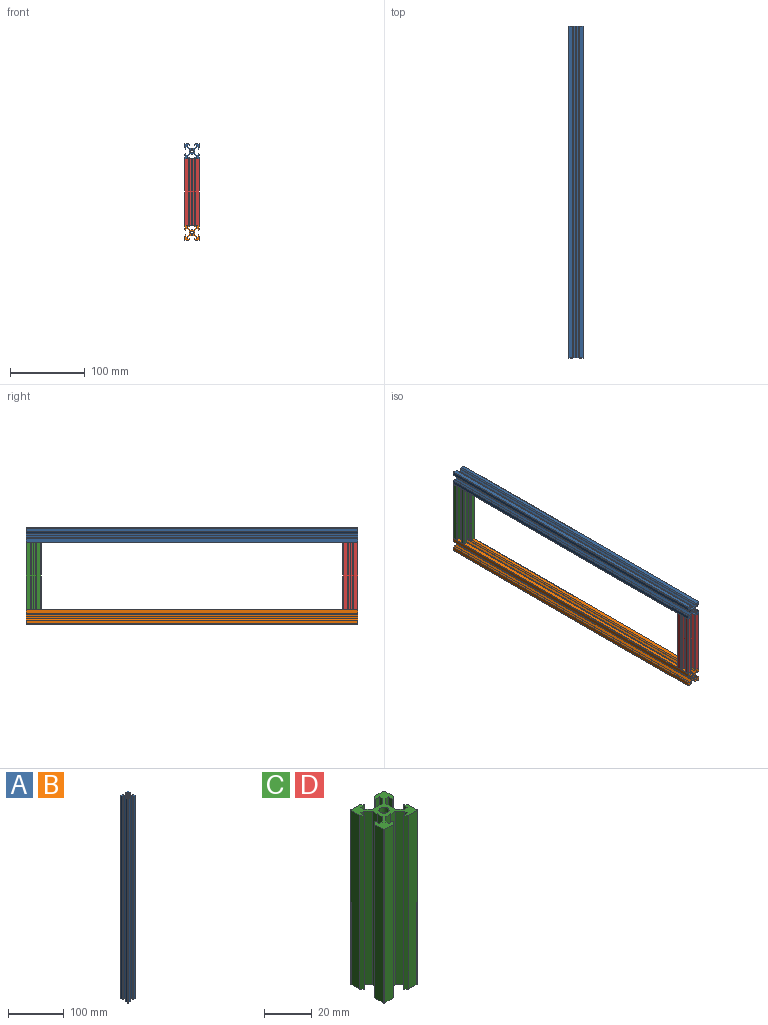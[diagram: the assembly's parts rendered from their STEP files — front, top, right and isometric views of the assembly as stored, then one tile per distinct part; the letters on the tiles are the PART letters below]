
ASSEMBLY  parts=4 mates=11
PART A: 71 faces, bbox 20x20x444.5 mm
  f0: cylinder r=2.1mm len=444.5mm, axis (0,0,-1), area 5865mm2, adj f69,f70
  f1: plane 444.5x0.21mm, normal (0.71,0.71,0), area 132mm2, adj f2,f68,f69,f70
  f2: plane 444.5x0.21mm, normal (0.71,-0.71,0), area 132mm2, adj f1,f3,f69,f70
  f3: plane 444.5x2.63mm, normal (1,0,0), area 1168.7mm2, adj f2,f4,f69,f70
  f4: plane 444.5x2.66mm, normal (0.71,-0.71,0), area 1672.5mm2, adj f3,f5,f69,f70
  f5: plane 444.5x1.64mm, normal (0,-1,0), area 728.7mm2, adj f4,f6,f69,f70
  f6: plane 444.5x2.38mm, normal (-1,0,0), area 1055.7mm2, adj f5,f7,f69,f70
  f7: plane 444.5x0.35mm, normal (0,-1,0), area 153.4mm2, adj f6,f8,f69,f70
  f8: plane 444.5x1.46mm, normal (0.71,-0.71,0), area 914.6mm2, adj f7,f9,f69,f70
  f9: plane 444.5x4.92mm, normal (1,0,0), area 2186.9mm2, adj f8,f10,f69,f70
  f10: cylinder r=0.5mm len=444.5mm, axis (0,0,-1), area 349.1mm2, adj f9,f11,f69,f70
  f11: plane 444.5x4.92mm, normal (0,1,0), area 2186.9mm2, adj f10,f12,f69,f70
  f12: plane 444.5x1.46mm, normal (-0.71,0.71,0), area 914.6mm2, adj f11,f13,f69,f70
  f13: plane 444.5x0.35mm, normal (-1,0,0), area 153.4mm2, adj f12,f14,f69,f70
  f14: plane 444.5x2.38mm, normal (0,-1,0), area 1055.7mm2, adj f13,f15,f69,f70
  f15: plane 444.5x1.64mm, normal (-1,0,0), area 728.7mm2, adj f14,f16,f69,f70
  f16: plane 444.5x2.66mm, normal (-0.71,0.71,0), area 1672.5mm2, adj f15,f17,f69,f70
  f17: plane 444.5x2.63mm, normal (0,1,0), area 1168.7mm2, adj f16,f18,f69,f70
  f18: plane 444.5x0.21mm, normal (-0.71,0.71,0), area 132mm2, adj f17,f19,f69,f70
  f19: plane 444.5x0.21mm, normal (0.71,0.71,0), area 132mm2, adj f18,f20,f69,f70
  f20: plane 444.5x2.63mm, normal (0,1,0), area 1168.7mm2, adj f19,f21,f69,f70
  f21: plane 444.5x2.66mm, normal (0.71,0.71,0), area 1672.5mm2, adj f20,f22,f69,f70
  f22: plane 444.5x1.64mm, normal (1,0,0), area 728.7mm2, adj f21,f23,f69,f70
  f23: plane 444.5x2.38mm, normal (0,-1,0), area 1055.7mm2, adj f22,f24,f69,f70
  f24: plane 444.5x0.35mm, normal (1,0,0), area 153.4mm2, adj f23,f25,f69,f70
  f25: plane 444.5x1.46mm, normal (0.71,0.71,0), area 914.6mm2, adj f24,f26,f69,f70
  f26: plane 444.5x4.92mm, normal (0,1,0), area 2186.9mm2, adj f25,f27,f69,f70
  f27: cylinder r=0.5mm len=444.5mm, axis (0,0,-1), area 349.1mm2, adj f26,f28,f69,f70
  f28: plane 444.5x4.92mm, normal (-1,0,0), area 2186.9mm2, adj f27,f29,f69,f70
  f29: plane 444.5x1.46mm, normal (-0.71,-0.71,0), area 914.6mm2, adj f28,f30,f69,f70
  f30: plane 444.5x0.35mm, normal (0,-1,0), area 153.4mm2, adj f29,f31,f69,f70
  f31: plane 444.5x2.38mm, normal (1,0,0), area 1055.7mm2, adj f30,f32,f69,f70
  f32: plane 444.5x1.64mm, normal (0,-1,0), area 728.7mm2, adj f31,f33,f69,f70
  f33: plane 444.5x2.66mm, normal (-0.71,-0.71,0), area 1672.5mm2, adj f32,f34,f69,f70
  f34: plane 444.5x2.63mm, normal (-1,0,0), area 1168.7mm2, adj f33,f35,f69,f70
  f35: plane 444.5x0.21mm, normal (-0.71,-0.71,0), area 132mm2, adj f34,f36,f69,f70
  f36: plane 444.5x0.21mm, normal (-0.71,0.71,0), area 132mm2, adj f35,f37,f69,f70
  f37: plane 444.5x2.63mm, normal (-1,0,0), area 1168.7mm2, adj f36,f38,f69,f70
  f38: plane 444.5x2.66mm, normal (-0.71,0.71,0), area 1672.5mm2, adj f37,f39,f69,f70
  f39: plane 444.5x1.64mm, normal (0,1,0), area 728.7mm2, adj f38,f40,f69,f70
  f40: plane 444.5x2.38mm, normal (1,0,0), area 1055.7mm2, adj f39,f41,f69,f70
  f41: plane 444.5x0.35mm, normal (0,1,0), area 153.4mm2, adj f40,f42,f69,f70
  f42: plane 444.5x1.46mm, normal (-0.71,0.71,0), area 914.6mm2, adj f41,f43,f69,f70
  f43: plane 444.5x4.92mm, normal (-1,0,0), area 2186.9mm2, adj f42,f44,f69,f70
  f44: cylinder r=0.5mm len=444.5mm, axis (0,0,-1), area 349.1mm2, adj f43,f45,f69,f70
  f45: plane 444.5x4.92mm, normal (0,-1,0), area 2186.9mm2, adj f44,f46,f69,f70
  f46: plane 444.5x1.46mm, normal (0.71,-0.71,0), area 914.6mm2, adj f45,f47,f69,f70
  f47: plane 444.5x0.35mm, normal (1,0,0), area 153.4mm2, adj f46,f48,f69,f70
  f48: plane 444.5x2.38mm, normal (0,1,0), area 1055.7mm2, adj f47,f49,f69,f70
  f49: plane 444.5x1.64mm, normal (1,0,0), area 728.7mm2, adj f48,f50,f69,f70
  f50: plane 444.5x2.66mm, normal (0.71,-0.71,0), area 1672.5mm2, adj f49,f51,f69,f70
  f51: plane 444.5x2.63mm, normal (0,-1,0), area 1168.7mm2, adj f50,f52,f69,f70
  f52: plane 444.5x0.21mm, normal (0.71,-0.71,0), area 132mm2, adj f51,f53,f69,f70
  f53: plane 444.5x0.21mm, normal (-0.71,-0.71,0), area 132mm2, adj f52,f54,f69,f70
  f54: plane 444.5x2.63mm, normal (0,-1,0), area 1168.7mm2, adj f53,f55,f69,f70
  f55: plane 444.5x2.66mm, normal (-0.71,-0.71,0), area 1672.5mm2, adj f54,f56,f69,f70
  f56: plane 444.5x1.64mm, normal (-1,0,0), area 728.7mm2, adj f55,f57,f69,f70
  f57: plane 444.5x2.38mm, normal (0,1,0), area 1055.7mm2, adj f56,f58,f69,f70
  f58: plane 444.5x0.35mm, normal (-1,0,0), area 153.4mm2, adj f57,f59,f69,f70
  f59: plane 444.5x1.46mm, normal (-0.71,-0.71,0), area 914.6mm2, adj f58,f60,f69,f70
  f60: plane 444.5x4.92mm, normal (0,-1,0), area 2186.9mm2, adj f59,f61,f69,f70
  f61: cylinder r=0.5mm len=444.5mm, axis (0,0,-1), area 349.1mm2, adj f60,f62,f69,f70
  f62: plane 444.5x4.92mm, normal (1,0,0), area 2186.9mm2, adj f61,f63,f69,f70
  f63: plane 444.5x1.46mm, normal (0.71,0.71,0), area 914.6mm2, adj f62,f64,f69,f70
  f64: plane 444.5x0.35mm, normal (0,1,0), area 153.4mm2, adj f63,f65,f69,f70
  f65: plane 444.5x2.38mm, normal (-1,0,0), area 1055.7mm2, adj f64,f66,f69,f70
  f66: plane 444.5x1.64mm, normal (0,1,0), area 728.7mm2, adj f65,f67,f69,f70
  f67: plane 444.5x2.66mm, normal (0.71,0.71,0), area 1672.5mm2, adj f66,f68,f69,f70
  f68: plane 444.5x2.63mm, normal (1,0,0), area 1168.7mm2, adj f1,f67,f69,f70
  f69: plane 20x20mm, normal (0,0,-1), area 171.4mm2, adj f0,f1,f2,f3,f4,f5,f6,f7
  f70: plane 20x20mm, normal (0,0,1), area 171.4mm2, adj f0,f1,f2,f3,f4,f5,f6,f7
PART B: same geometry as A
PART C: 71 faces, bbox 20x20x88.9 mm
  f0: cylinder r=2.1mm len=88.9mm, axis (0,0,-1), area 1173mm2, adj f69,f70
  f1: plane 88.9x0.21mm, normal (0.71,0.71,0), area 26.4mm2, adj f2,f68,f69,f70
  f2: plane 88.9x0.21mm, normal (0.71,-0.71,0), area 26.4mm2, adj f1,f3,f69,f70
  f3: plane 88.9x2.63mm, normal (1,0,0), area 233.7mm2, adj f2,f4,f69,f70
  f4: plane 88.9x2.66mm, normal (0.71,-0.71,0), area 334.5mm2, adj f3,f5,f69,f70
  f5: plane 88.9x1.64mm, normal (0,-1,0), area 145.7mm2, adj f4,f6,f69,f70
  f6: plane 88.9x2.38mm, normal (-1,0,0), area 211.1mm2, adj f5,f7,f69,f70
  f7: plane 88.9x0.35mm, normal (0,-1,0), area 30.7mm2, adj f6,f8,f69,f70
  f8: plane 88.9x1.46mm, normal (0.71,-0.71,0), area 182.9mm2, adj f7,f9,f69,f70
  f9: plane 88.9x4.92mm, normal (1,0,0), area 437.4mm2, adj f8,f10,f69,f70
  f10: cylinder r=0.5mm len=88.9mm, axis (0,0,-1), area 69.8mm2, adj f9,f11,f69,f70
  f11: plane 88.9x4.92mm, normal (0,1,0), area 437.4mm2, adj f10,f12,f69,f70
  f12: plane 88.9x1.46mm, normal (-0.71,0.71,0), area 182.9mm2, adj f11,f13,f69,f70
  f13: plane 88.9x0.35mm, normal (-1,0,0), area 30.7mm2, adj f12,f14,f69,f70
  f14: plane 88.9x2.38mm, normal (0,-1,0), area 211.1mm2, adj f13,f15,f69,f70
  f15: plane 88.9x1.64mm, normal (-1,0,0), area 145.7mm2, adj f14,f16,f69,f70
  f16: plane 88.9x2.66mm, normal (-0.71,0.71,0), area 334.5mm2, adj f15,f17,f69,f70
  f17: plane 88.9x2.63mm, normal (0,1,0), area 233.7mm2, adj f16,f18,f69,f70
  f18: plane 88.9x0.21mm, normal (-0.71,0.71,0), area 26.4mm2, adj f17,f19,f69,f70
  f19: plane 88.9x0.21mm, normal (0.71,0.71,0), area 26.4mm2, adj f18,f20,f69,f70
  f20: plane 88.9x2.63mm, normal (0,1,0), area 233.7mm2, adj f19,f21,f69,f70
  f21: plane 88.9x2.66mm, normal (0.71,0.71,0), area 334.5mm2, adj f20,f22,f69,f70
  f22: plane 88.9x1.64mm, normal (1,0,0), area 145.7mm2, adj f21,f23,f69,f70
  f23: plane 88.9x2.38mm, normal (0,-1,0), area 211.1mm2, adj f22,f24,f69,f70
  f24: plane 88.9x0.35mm, normal (1,0,0), area 30.7mm2, adj f23,f25,f69,f70
  f25: plane 88.9x1.46mm, normal (0.71,0.71,0), area 182.9mm2, adj f24,f26,f69,f70
  f26: plane 88.9x4.92mm, normal (0,1,0), area 437.4mm2, adj f25,f27,f69,f70
  f27: cylinder r=0.5mm len=88.9mm, axis (0,0,-1), area 69.8mm2, adj f26,f28,f69,f70
  f28: plane 88.9x4.92mm, normal (-1,0,0), area 437.4mm2, adj f27,f29,f69,f70
  f29: plane 88.9x1.46mm, normal (-0.71,-0.71,0), area 182.9mm2, adj f28,f30,f69,f70
  f30: plane 88.9x0.35mm, normal (0,-1,0), area 30.7mm2, adj f29,f31,f69,f70
  f31: plane 88.9x2.38mm, normal (1,0,0), area 211.1mm2, adj f30,f32,f69,f70
  f32: plane 88.9x1.64mm, normal (0,-1,0), area 145.7mm2, adj f31,f33,f69,f70
  f33: plane 88.9x2.66mm, normal (-0.71,-0.71,0), area 334.5mm2, adj f32,f34,f69,f70
  f34: plane 88.9x2.63mm, normal (-1,0,0), area 233.7mm2, adj f33,f35,f69,f70
  f35: plane 88.9x0.21mm, normal (-0.71,-0.71,0), area 26.4mm2, adj f34,f36,f69,f70
  f36: plane 88.9x0.21mm, normal (-0.71,0.71,0), area 26.4mm2, adj f35,f37,f69,f70
  f37: plane 88.9x2.63mm, normal (-1,0,0), area 233.7mm2, adj f36,f38,f69,f70
  f38: plane 88.9x2.66mm, normal (-0.71,0.71,0), area 334.5mm2, adj f37,f39,f69,f70
  f39: plane 88.9x1.64mm, normal (0,1,0), area 145.7mm2, adj f38,f40,f69,f70
  f40: plane 88.9x2.38mm, normal (1,0,0), area 211.1mm2, adj f39,f41,f69,f70
  f41: plane 88.9x0.35mm, normal (0,1,0), area 30.7mm2, adj f40,f42,f69,f70
  f42: plane 88.9x1.46mm, normal (-0.71,0.71,0), area 182.9mm2, adj f41,f43,f69,f70
  f43: plane 88.9x4.92mm, normal (-1,0,0), area 437.4mm2, adj f42,f44,f69,f70
  f44: cylinder r=0.5mm len=88.9mm, axis (0,0,-1), area 69.8mm2, adj f43,f45,f69,f70
  f45: plane 88.9x4.92mm, normal (0,-1,0), area 437.4mm2, adj f44,f46,f69,f70
  f46: plane 88.9x1.46mm, normal (0.71,-0.71,0), area 182.9mm2, adj f45,f47,f69,f70
  f47: plane 88.9x0.35mm, normal (1,0,0), area 30.7mm2, adj f46,f48,f69,f70
  f48: plane 88.9x2.38mm, normal (0,1,0), area 211.1mm2, adj f47,f49,f69,f70
  f49: plane 88.9x1.64mm, normal (1,0,0), area 145.7mm2, adj f48,f50,f69,f70
  f50: plane 88.9x2.66mm, normal (0.71,-0.71,0), area 334.5mm2, adj f49,f51,f69,f70
  f51: plane 88.9x2.63mm, normal (0,-1,0), area 233.7mm2, adj f50,f52,f69,f70
  f52: plane 88.9x0.21mm, normal (0.71,-0.71,0), area 26.4mm2, adj f51,f53,f69,f70
  f53: plane 88.9x0.21mm, normal (-0.71,-0.71,0), area 26.4mm2, adj f52,f54,f69,f70
  f54: plane 88.9x2.63mm, normal (0,-1,0), area 233.7mm2, adj f53,f55,f69,f70
  f55: plane 88.9x2.66mm, normal (-0.71,-0.71,0), area 334.5mm2, adj f54,f56,f69,f70
  f56: plane 88.9x1.64mm, normal (-1,0,0), area 145.7mm2, adj f55,f57,f69,f70
  f57: plane 88.9x2.38mm, normal (0,1,0), area 211.1mm2, adj f56,f58,f69,f70
  f58: plane 88.9x0.35mm, normal (-1,0,0), area 30.7mm2, adj f57,f59,f69,f70
  f59: plane 88.9x1.46mm, normal (-0.71,-0.71,0), area 182.9mm2, adj f58,f60,f69,f70
  f60: plane 88.9x4.92mm, normal (0,-1,0), area 437.4mm2, adj f59,f61,f69,f70
  f61: cylinder r=0.5mm len=88.9mm, axis (0,0,-1), area 69.8mm2, adj f60,f62,f69,f70
  f62: plane 88.9x4.92mm, normal (1,0,0), area 437.4mm2, adj f61,f63,f69,f70
  f63: plane 88.9x1.46mm, normal (0.71,0.71,0), area 182.9mm2, adj f62,f64,f69,f70
  f64: plane 88.9x0.35mm, normal (0,1,0), area 30.7mm2, adj f63,f65,f69,f70
  f65: plane 88.9x2.38mm, normal (-1,0,0), area 211.1mm2, adj f64,f66,f69,f70
  f66: plane 88.9x1.64mm, normal (0,1,0), area 145.7mm2, adj f65,f67,f69,f70
  f67: plane 88.9x2.66mm, normal (0.71,0.71,0), area 334.5mm2, adj f66,f68,f69,f70
  f68: plane 88.9x2.63mm, normal (1,0,0), area 233.7mm2, adj f1,f67,f69,f70
  f69: plane 20x20mm, normal (0,0,-1), area 171.4mm2, adj f0,f1,f2,f3,f4,f5,f6,f7
  f70: plane 20x20mm, normal (0,0,1), area 171.4mm2, adj f0,f1,f2,f3,f4,f5,f6,f7
PART D: same geometry as C
PLACE A rot(axis=(0.58,0.58,-0.58),120deg) t=(-3.08,449.05,114.4)mm
PLACE B rot(axis=(-1,0,0),90deg) t=(-3.08,4.55,5.5)mm fixed
PLACE C t=(-3.08,439.05,15.5)mm
PLACE D t=(-3.08,14.55,15.5)mm
MATE planar D.f45 <-> B.f69  axis (0,-1,0) through (-10.12,4.55,59.95)mm
MATE planar D.f43 <-> B.f43  axis (-1,0,0) through (-13.08,7.51,59.95)mm
MATE planar C.f0 <-> A.f62  axis (0,0,1) through (-3.08,439.05,104.4)mm
MATE planar D.f45 <-> A.f0  axis (0,-1,0) through (-10.12,4.55,104.4)mm
MATE planar B.f45 <-> D.f0  axis (0,0,1) through (-10.12,226.8,15.5)mm
MATE planar D.f62 <-> A.f11  axis (1,0,0) through (6.92,7.51,59.95)mm
MATE cylindrical B.f69 <-> B.f0  axis (0,1,0) through (-5.92,4.55,1.6)mm
MATE planar C.f43 <-> A.f60  axis (-1,0,0) through (-13.08,432.01,59.95)mm
MATE planar A.f62 <-> D.f0  axis (0,0,-1) through (-10.12,226.8,104.4)mm
MATE planar C.f26 <-> A.f0  axis (0,1,0) through (-10.12,449.05,59.95)mm
MATE planar B.f69 <-> B.f0  axis (0,-1,0) through (-6.98,4.55,2.66)mm
